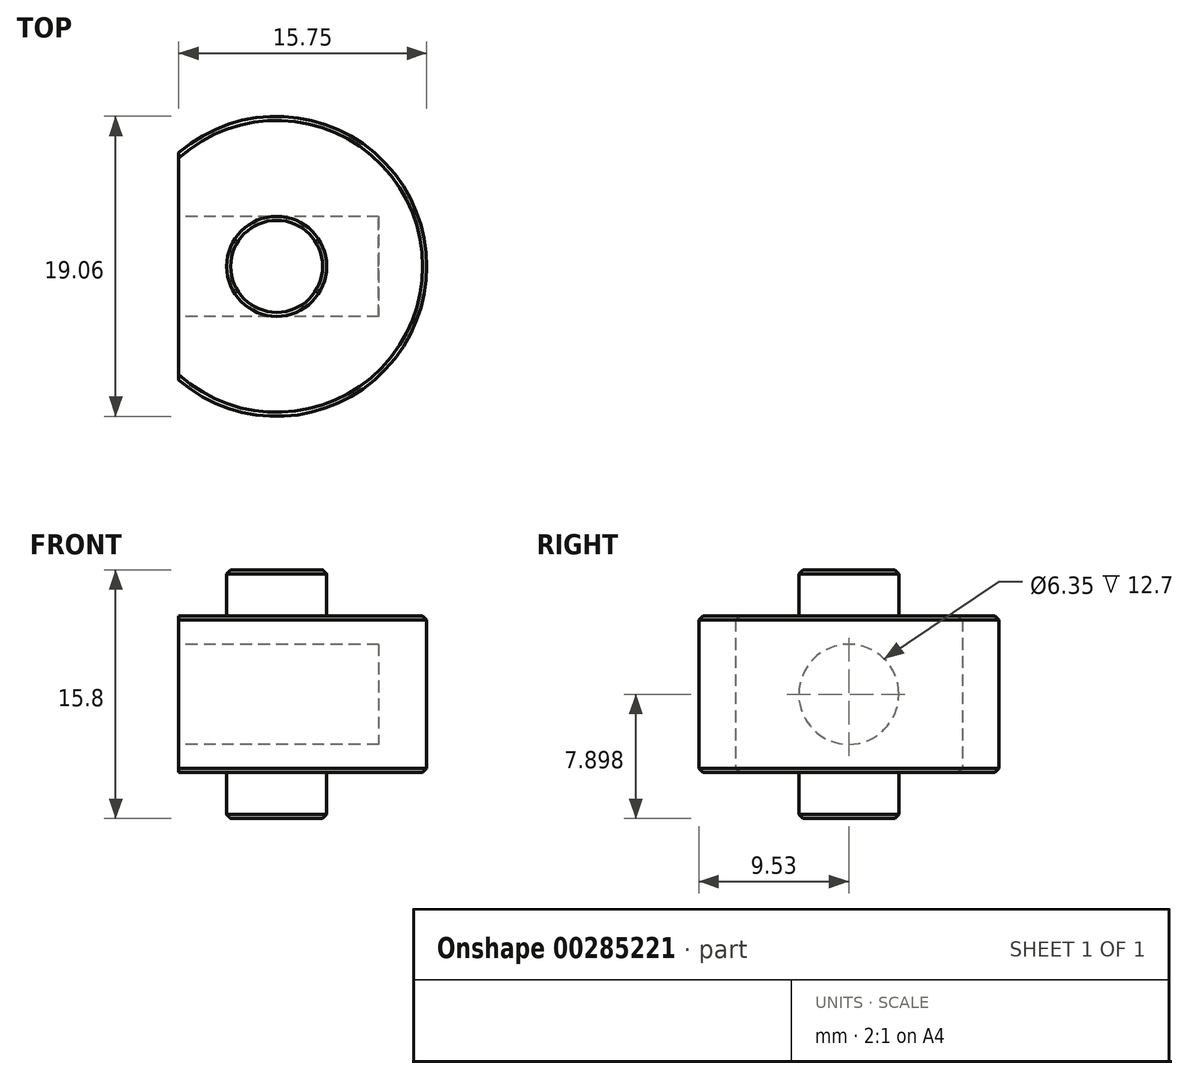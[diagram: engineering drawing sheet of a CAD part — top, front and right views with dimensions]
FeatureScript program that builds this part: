
annotation { "Feature Type Name" : "Feature", "Feature Type Description" : "" }
export const myFeature = defineFeature(function(context is Context, id is Id, definition is map)
    precondition{}
    {
        {
            var Q0;
            Q0=qCreatedBy(makeId("Top.planeOp"),FACE);
            var sketch = newSketch(context, id + "F0", { "sketchPlane" : qUnion([Q0])});
            skArc(sketch, "E0", {"start": v(-6.22, -7.21) * mm, "mid": v(9.52, 0) * mm, "end": v(-6.22, 7.21) * mm});
            skLineSegment(sketch, "E1", {"start": v(-6.22, -7.21) * mm, "end": v(-6.22, 7.21) * mm});
            skSolve(sketch);
        }
        {
            var Q0;
            Q0 = qSketchRegion(id + "F0", true);
            extrude(context, id + "F1", {"entities" : qUnion([Q0]), "depth" : 9.96 * mm});
        }
        {
            var Q0;
            Q0=makeQuery(id+"F1.opExtrude","CAP_FACE",FACE,{"disambiguationData":[OSD([sQuery(id+"F0.wireOp",EDGE,"E0")])],"isStart":false});
            var sketch = newSketch(context, id + "F2", { "sketchPlane" : qUnion([Q0])});
            skCircle(sketch, "E2", {"center": v(0, 0) * mm, "radius": 3.18 * mm});
            skSolve(sketch);
        }
        {
            var Q0;
            Q0 = qSketchRegion(id + "F2", true);
            extrude(context, id + "F3", {"entities" : qUnion([Q0]), "operationType" : NewBodyOperationType.ADD, "depth" : 2.92 * mm});
        }
        {
            var Q0;
            Q0=makeQuery(id+"F1.opExtrude","CAP_FACE",FACE,{"disambiguationData":[OSD([sQuery(id+"F0.wireOp",EDGE,"E0")])],"isStart":true});
            var sketch = newSketch(context, id + "F4", { "sketchPlane" : qUnion([Q0])});
            skCircle(sketch, "E3", {"center": v(0, 0) * mm, "radius": 3.18 * mm});
            skSolve(sketch);
        }
        {
            var Q0;
            Q0=makeQuery(id+"F4.imprint","IMPRINT",FACE,{"disambiguationData":[TD([[makeQuery(id+"F4.imprint","IMPRINT",EDGE,{"derivedFrom":sQuery(id+"F4.wireOp",EDGE,"E3")}),1.0]])]});
            extrude(context, id + "F5", {"entities" : qUnion([Q0]), "operationType" : NewBodyOperationType.ADD, "depth" : 2.92 * mm});
        }
        {
            var Q0;
            Q0=makeQuery(id+"F1.opExtrude","SWEPT_FACE",FACE,{"disambiguationData":[OSD([sQuery(id+"F0.wireOp",EDGE,"E1")])]});
            var sketch = newSketch(context, id + "F6", { "sketchPlane" : qUnion([Q0])});
            skLineSegment(sketch, "E4.0.0", {"start": v(-7.21, 0) * mm, "end": v(7.21, 0) * mm});
            skLineSegment(sketch, "E4.0.1", {"start": v(7.21, 0) * mm, "end": v(7.21, 9.96) * mm});
            skLineSegment(sketch, "E4.0.2", {"start": v(7.21, 9.96) * mm, "end": v(-7.21, 9.96) * mm});
            skLineSegment(sketch, "E4.0.3", {"start": v(-7.21, 9.96) * mm, "end": v(-7.21, 0) * mm});
            skLineSegment(sketch, "E5", {"start": v(7.21, 9.96) * mm, "end": v(-7.21, 0) * mm, "construction": true});
            skCircle(sketch, "E6", {"center": v(0, 4.98) * mm, "radius": 3.18 * mm});
            skSolve(sketch);
        }
        {
            var Q0;
            Q0=makeQuery(id+"F6.imprint","IMPRINT",FACE,{"disambiguationData":[TD([[makeQuery(id+"F6.imprint","IMPRINT",EDGE,{"derivedFrom":sQuery(id+"F6.wireOp",EDGE,"E6")}),1.0]])]});
            extrude(context, id + "F7", {"entities" : qUnion([Q0]), "operationType" : NewBodyOperationType.REMOVE, "oppositeDirection" : true, "depth" : 12.7 * mm});
        }
        {
            var Q0;
            Q0=makeQuery(id+"F3.opExtrude","CAP_EDGE",EDGE,{"disambiguationData":[OSD([sQuery(id+"F2.wireOp",EDGE,"E2")])],"isStart":false});
            var Q1;
            Q1=makeQuery(id+"F1.opExtrude","CAP_EDGE",EDGE,{"disambiguationData":[OSD([sQuery(id+"F0.wireOp",EDGE,"E0")])],"isStart":false});
            var Q2;
            Q2=makeQuery(id+"F1.opExtrude","CAP_EDGE",EDGE,{"disambiguationData":[OSD([sQuery(id+"F0.wireOp",EDGE,"E0")])],"isStart":true});
            var Q3;
            Q3=makeQuery(id+"F5.opExtrude","CAP_EDGE",EDGE,{"disambiguationData":[OSD([sQuery(id+"F4.wireOp",EDGE,"E3")])],"isStart":false});
            chamfer(context, id + "F8", {"entities" : qUnion([Q0, Q1, Q2, Q3]), "width" : 0.25 * mm, "tangentPropagation" : true});
        }
    });
